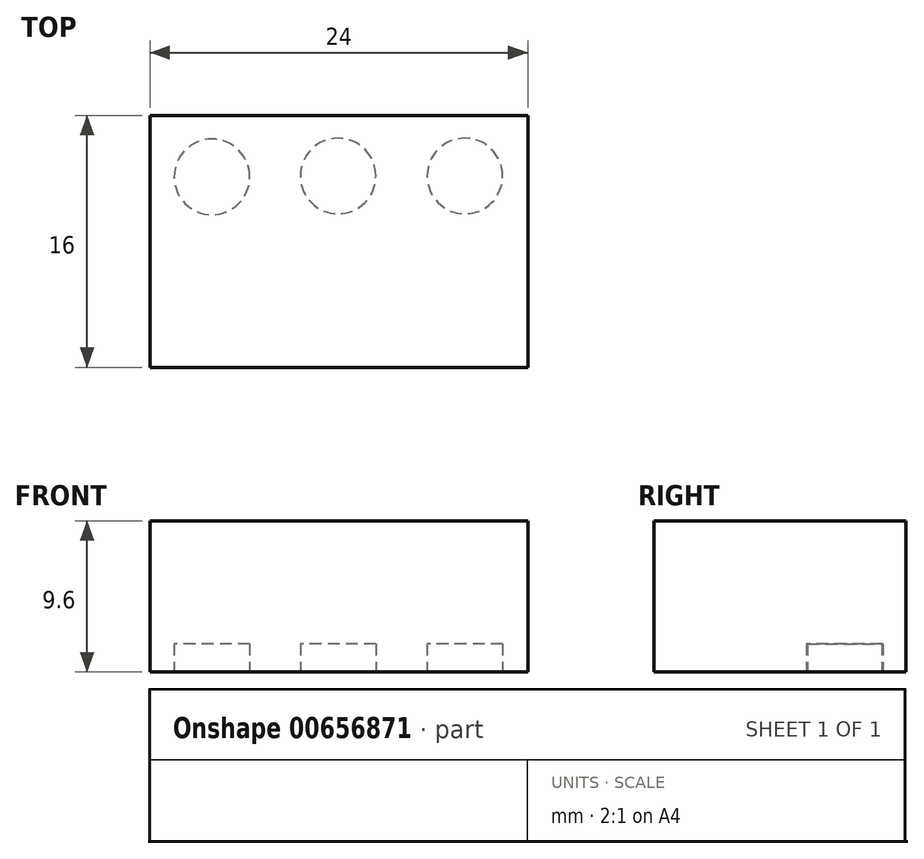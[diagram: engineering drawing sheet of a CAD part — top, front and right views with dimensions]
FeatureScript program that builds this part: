
annotation { "Feature Type Name" : "Feature", "Feature Type Description" : "" }
export const myFeature = defineFeature(function(context is Context, id is Id, definition is map)
    precondition{}
    {
        {
            var Q0;
            Q0=qCreatedBy(makeId("Top.planeOp"),FACE);
            var sketch = newSketch(context, id + "F0", { "sketchPlane" : qUnion([Q0])});
            skLineSegment(sketch, "E0.bottom", {"start": v(0, 0) * mm, "end": v(-24, 0) * mm});
            skLineSegment(sketch, "E0.top", {"start": v(0, 16) * mm, "end": v(-24, 16) * mm});
            skLineSegment(sketch, "E0.left", {"start": v(0, 0) * mm, "end": v(0, 16) * mm});
            skLineSegment(sketch, "E0.right", {"start": v(-24, 0) * mm, "end": v(-24, 16) * mm});
            skSolve(sketch);
        }
        {
            var Q0;
            Q0=makeQuery(id+"F0.imprint","IMPRINT",FACE,{"disambiguationData":[TD([[makeQuery(id+"F0.imprint","IMPRINT",EDGE,{"derivedFrom":sQuery(id+"F0.wireOp",EDGE,"E0.bottom")}),-1.0]])]});
            extrude(context, id + "F1", {"entities" : qUnion([Q0]), "depth" : 9.6 * mm, "offsetDistance" : 25.4 * mm});
        }
        {
            var Q0;
            Q0=qCreatedBy(makeId("Top.planeOp"),FACE);
            var sketch = newSketch(context, id + "F2", { "sketchPlane" : qUnion([Q0])});
            skLineSegment(sketch, "E1", {"start": v(-32.22, 8.12) * mm, "end": v(0, 8.12) * mm, "construction": true});
            skLineSegment(sketch, "E2", {"start": v(-16, 21.64) * mm, "end": v(-16, 0) * mm, "construction": true});
            skLineSegment(sketch, "E3", {"start": v(-8, 21.64) * mm, "end": v(-8, 0) * mm, "construction": true});
            skLineSegment(sketch, "E4", {"start": v(-24.02, 16.08) * mm, "end": v(-16.11, 8.12) * mm, "construction": true});
            skLineSegment(sketch, "E5", {"start": v(-16.11, 8.12) * mm, "end": v(-8, 16.19) * mm, "construction": true});
            skLineSegment(sketch, "E6", {"start": v(-8, 16.19) * mm, "end": v(0, 8.12) * mm, "construction": true});
            skCircle(sketch, "E7", {"center": v(-20.07, 12.1) * mm, "radius": 2.4 * mm});
            skCircle(sketch, "E8", {"center": v(-12.06, 12.15) * mm, "radius": 2.4 * mm});
            skCircle(sketch, "E9", {"center": v(-4, 12.15) * mm, "radius": 2.4 * mm});
            skCircle(sketch, "E10.MirrorC", {"center": v(-20.07, 4.14) * mm, "radius": 2.4 * mm});
            skCircle(sketch, "E11.MirrorC", {"center": v(-12.06, 4.1) * mm, "radius": 2.4 * mm});
            skCircle(sketch, "E12.MirrorC", {"center": v(-4, 4.1) * mm, "radius": 2.4 * mm});
            skSolve(sketch);
        }
        {
            var Q0;
            Q0=makeQuery(id+"F2.imprint","IMPRINT",FACE,{"disambiguationData":[TD([[makeQuery(id+"F2.imprint","IMPRINT",EDGE,{"derivedFrom":sQuery(id+"F2.wireOp",EDGE,"E9")}),1.0]])]});
            var Q1;
            Q1=makeQuery(id+"F2.imprint","IMPRINT",FACE,{"disambiguationData":[TD([[makeQuery(id+"F2.imprint","IMPRINT",EDGE,{"derivedFrom":sQuery(id+"F2.wireOp",EDGE,"E8")}),1.0]])]});
            var Q2;
            Q2=makeQuery(id+"F2.imprint","IMPRINT",FACE,{"disambiguationData":[TD([[makeQuery(id+"F2.imprint","IMPRINT",EDGE,{"derivedFrom":sQuery(id+"F2.wireOp",EDGE,"E7")}),1.0]])]});
            var Q3;
            Q3=makeQuery(id+"F2.imprint","IMPRINT",FACE,{"disambiguationData":[TD([[makeQuery(id+"F2.imprint","IMPRINT",EDGE,{"derivedFrom":sQuery(id+"F2.wireOp",EDGE,"E10.MirrorC")}),-1.0]])]});
            var Q4;
            Q4=makeQuery(id+"F2.imprint","IMPRINT",FACE,{"disambiguationData":[TD([[makeQuery(id+"F2.imprint","IMPRINT",EDGE,{"derivedFrom":sQuery(id+"F2.wireOp",EDGE,"E11.MirrorC")}),-1.0]])]});
            var Q5;
            Q5=makeQuery(id+"F2.imprint","IMPRINT",FACE,{"disambiguationData":[TD([[makeQuery(id+"F2.imprint","IMPRINT",EDGE,{"derivedFrom":sQuery(id+"F2.wireOp",EDGE,"E12.MirrorC")}),-1.0]])]});
            extrude(context, id + "F3", {"entities" : qUnion([Q0, Q1, Q2, Q3, Q4, Q5]), "depth" : 1.8 * mm, "offsetDistance" : 25.4 * mm});
        }
    });
